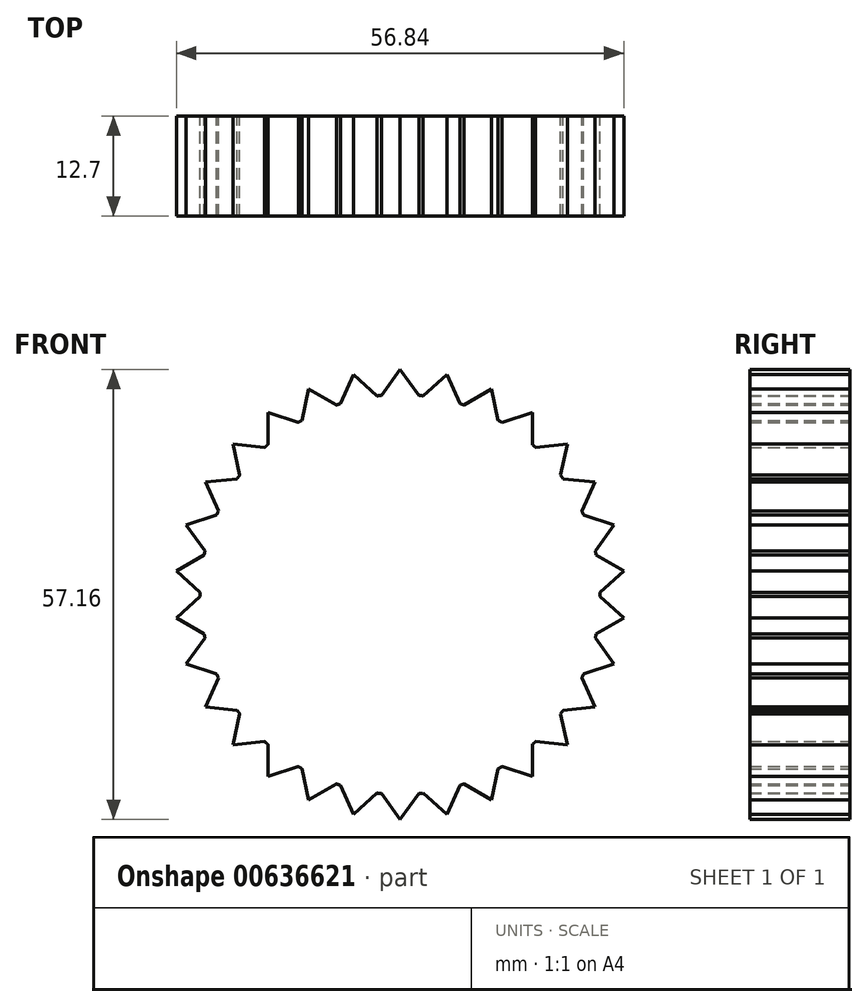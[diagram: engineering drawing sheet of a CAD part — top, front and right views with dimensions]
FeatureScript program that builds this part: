
annotation { "Feature Type Name" : "Feature", "Feature Type Description" : "" }
export const myFeature = defineFeature(function(context is Context, id is Id, definition is map)
    precondition{}
    {
        {
            var Q0;
            Q0=qCreatedBy(makeId("Front.planeOp"),FACE);
            var sketch = newSketch(context, id + "F0", { "sketchPlane" : qUnion([Q0])});
            skCircle(sketch, "E0", {"center": v(0, 0) * mm, "radius": 25.4 * mm});
            skLineSegment(sketch, "E1", {"start": v(0, 25.4) * mm, "end": v(0, 28.58) * mm});
            skLineSegment(sketch, "E2", {"start": v(0, 28.58) * mm, "end": v(2.38, 25.29) * mm});
            skLineSegment(sketch, "E3.MirrorCS", {"start": v(0, 28.58) * mm, "end": v(-2.38, 25.29) * mm});
            skLineSegment(sketch, "E4.1.0", {"start": v(-5.94, 27.95) * mm, "end": v(-2.93, 25.23) * mm});
            skLineSegment(sketch, "E4.1.1", {"start": v(-5.94, 27.95) * mm, "end": v(-7.59, 24.24) * mm});
            skLineSegment(sketch, "E4.2.0", {"start": v(-11.62, 26.1) * mm, "end": v(-8.11, 24.07) * mm});
            skLineSegment(sketch, "E4.2.1", {"start": v(-11.62, 26.1) * mm, "end": v(-12.46, 22.13) * mm});
            skLineSegment(sketch, "E4.3.0", {"start": v(-16.8, 23.12) * mm, "end": v(-12.94, 21.86) * mm});
            skLineSegment(sketch, "E4.3.1", {"start": v(-16.8, 23.12) * mm, "end": v(-16.79, 19.06) * mm});
            skLineSegment(sketch, "E4.4.0", {"start": v(-21.24, 19.12) * mm, "end": v(-17.2, 18.69) * mm});
            skLineSegment(sketch, "E4.4.1", {"start": v(-21.24, 19.12) * mm, "end": v(-20.39, 15.15) * mm});
            skLineSegment(sketch, "E4.5.0", {"start": v(-24.75, 14.29) * mm, "end": v(-20.71, 14.7) * mm});
            skLineSegment(sketch, "E4.5.1", {"start": v(-24.75, 14.29) * mm, "end": v(-23.1, 10.58) * mm});
            skLineSegment(sketch, "E4.6.0", {"start": v(-27.18, 8.83) * mm, "end": v(-23.32, 10.08) * mm});
            skLineSegment(sketch, "E4.6.1", {"start": v(-27.18, 8.83) * mm, "end": v(-24.79, 5.55) * mm});
            skLineSegment(sketch, "E4.7.0", {"start": v(-28.42, 2.99) * mm, "end": v(-24.9, 5.01) * mm});
            skLineSegment(sketch, "E4.7.1", {"start": v(-28.42, 2.99) * mm, "end": v(-25.4, 0.28) * mm});
            skLineSegment(sketch, "E4.8.0", {"start": v(-28.42, -2.99) * mm, "end": v(-25.4, -0.28) * mm});
            skLineSegment(sketch, "E4.8.1", {"start": v(-28.42, -2.99) * mm, "end": v(-24.9, -5.01) * mm});
            skLineSegment(sketch, "E4.9.0", {"start": v(-27.18, -8.83) * mm, "end": v(-24.79, -5.55) * mm});
            skLineSegment(sketch, "E4.9.1", {"start": v(-27.18, -8.83) * mm, "end": v(-23.32, -10.08) * mm});
            skLineSegment(sketch, "E4.10.0", {"start": v(-24.75, -14.29) * mm, "end": v(-23.1, -10.58) * mm});
            skLineSegment(sketch, "E4.10.1", {"start": v(-24.75, -14.29) * mm, "end": v(-20.71, -14.7) * mm});
            skLineSegment(sketch, "E4.11.0", {"start": v(-21.24, -19.12) * mm, "end": v(-20.39, -15.15) * mm});
            skLineSegment(sketch, "E4.11.1", {"start": v(-21.24, -19.12) * mm, "end": v(-17.2, -18.69) * mm});
            skLineSegment(sketch, "E4.12.0", {"start": v(-16.8, -23.12) * mm, "end": v(-16.79, -19.06) * mm});
            skLineSegment(sketch, "E4.12.1", {"start": v(-16.8, -23.12) * mm, "end": v(-12.94, -21.86) * mm});
            skLineSegment(sketch, "E4.13.0", {"start": v(-11.62, -26.1) * mm, "end": v(-12.46, -22.13) * mm});
            skLineSegment(sketch, "E4.13.1", {"start": v(-11.62, -26.1) * mm, "end": v(-8.11, -24.07) * mm});
            skLineSegment(sketch, "E4.14.0", {"start": v(-5.94, -27.95) * mm, "end": v(-7.59, -24.24) * mm});
            skLineSegment(sketch, "E4.14.1", {"start": v(-5.94, -27.95) * mm, "end": v(-2.93, -25.23) * mm});
            skLineSegment(sketch, "E4.15.0", {"start": v(0, -28.58) * mm, "end": v(-2.38, -25.29) * mm});
            skLineSegment(sketch, "E4.15.1", {"start": v(0, -28.58) * mm, "end": v(2.38, -25.29) * mm});
            skLineSegment(sketch, "E4.16.0", {"start": v(5.94, -27.95) * mm, "end": v(2.93, -25.23) * mm});
            skLineSegment(sketch, "E4.16.1", {"start": v(5.94, -27.95) * mm, "end": v(7.59, -24.24) * mm});
            skLineSegment(sketch, "E4.17.0", {"start": v(11.62, -26.1) * mm, "end": v(8.11, -24.07) * mm});
            skLineSegment(sketch, "E4.17.1", {"start": v(11.62, -26.1) * mm, "end": v(12.46, -22.13) * mm});
            skLineSegment(sketch, "E4.18.0", {"start": v(16.8, -23.12) * mm, "end": v(12.94, -21.86) * mm});
            skLineSegment(sketch, "E4.18.1", {"start": v(16.8, -23.12) * mm, "end": v(16.79, -19.06) * mm});
            skLineSegment(sketch, "E4.19.0", {"start": v(21.24, -19.12) * mm, "end": v(17.2, -18.69) * mm});
            skLineSegment(sketch, "E4.19.1", {"start": v(21.24, -19.12) * mm, "end": v(20.39, -15.15) * mm});
            skLineSegment(sketch, "E4.20.0", {"start": v(24.75, -14.29) * mm, "end": v(20.71, -14.7) * mm});
            skLineSegment(sketch, "E4.20.1", {"start": v(24.75, -14.29) * mm, "end": v(23.1, -10.58) * mm});
            skLineSegment(sketch, "E4.21.0", {"start": v(27.18, -8.83) * mm, "end": v(23.32, -10.08) * mm});
            skLineSegment(sketch, "E4.21.1", {"start": v(27.18, -8.83) * mm, "end": v(24.79, -5.55) * mm});
            skLineSegment(sketch, "E4.22.0", {"start": v(28.42, -2.99) * mm, "end": v(24.9, -5.01) * mm});
            skLineSegment(sketch, "E4.22.1", {"start": v(28.42, -2.99) * mm, "end": v(25.4, -0.28) * mm});
            skLineSegment(sketch, "E4.23.0", {"start": v(28.42, 2.99) * mm, "end": v(25.4, 0.28) * mm});
            skLineSegment(sketch, "E4.23.1", {"start": v(28.42, 2.99) * mm, "end": v(24.9, 5.01) * mm});
            skLineSegment(sketch, "E4.24.0", {"start": v(27.18, 8.83) * mm, "end": v(24.79, 5.55) * mm});
            skLineSegment(sketch, "E4.24.1", {"start": v(27.18, 8.83) * mm, "end": v(23.32, 10.08) * mm});
            skLineSegment(sketch, "E4.25.0", {"start": v(24.75, 14.29) * mm, "end": v(23.1, 10.58) * mm});
            skLineSegment(sketch, "E4.25.1", {"start": v(24.75, 14.29) * mm, "end": v(20.71, 14.7) * mm});
            skLineSegment(sketch, "E4.26.0", {"start": v(21.24, 19.12) * mm, "end": v(20.39, 15.15) * mm});
            skLineSegment(sketch, "E4.26.1", {"start": v(21.24, 19.12) * mm, "end": v(17.2, 18.69) * mm});
            skLineSegment(sketch, "E4.27.0", {"start": v(16.8, 23.12) * mm, "end": v(16.79, 19.06) * mm});
            skLineSegment(sketch, "E4.27.1", {"start": v(16.8, 23.12) * mm, "end": v(12.94, 21.86) * mm});
            skLineSegment(sketch, "E4.28.0", {"start": v(11.62, 26.1) * mm, "end": v(12.46, 22.13) * mm});
            skLineSegment(sketch, "E4.28.1", {"start": v(11.62, 26.1) * mm, "end": v(8.11, 24.07) * mm});
            skLineSegment(sketch, "E4.29.0", {"start": v(5.94, 27.95) * mm, "end": v(7.59, 24.24) * mm});
            skLineSegment(sketch, "E4.29.1", {"start": v(5.94, 27.95) * mm, "end": v(2.93, 25.23) * mm});
            skSolve(sketch);
        }
        {
            var Q0;
            Q0 = qSketchRegion(id + "F0", true);
            extrude(context, id + "F1", {"entities" : qUnion([Q0]), "depth" : 12.7 * mm, "offsetDistance" : 25.4 * mm});
        }
    });
